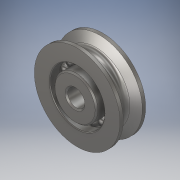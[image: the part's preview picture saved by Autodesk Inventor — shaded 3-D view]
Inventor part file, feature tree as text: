
AUTODESK INVENTOR PART (.ipt)
format: ipt  version: 2019.4 (Build 234330000, 330)  size: 734,208 bytes
history: native  units: in
note: dims shown in document units (in); Inventor stores cm internally (conversion verified against a paired STEP export)
features: other x14, chamfer x2, revolve x1
ambient origin geometry x8: Origin, YZ Plane, XZ Plane, XY Plane, X Axis, Y Axis, Z Axis, Center Point
bodies: Solid1 (feature_tree), Solid2 (feature_tree), Solid3 (feature_tree), Solid4 (feature_tree), Solid5 (feature_tree), Solid6 (feature_tree), Solid7 (feature_tree), Solid8 (feature_tree), Solid9 (feature_tree), Solid10 (feature_tree), Solid11 (feature_tree), Solid12 (feature_tree), Solid13 (feature_tree), Solid14 (feature_tree), Solid15 (feature_tree), Solid16 (feature_tree), Solid17 (feature_tree)
feature tree (17):
  chamfer  "Chamfer2"  [1 undecoded]
  chamfer  "Chamfer1"  [1 undecoded]
  revolve  "Revolve2"  [1 undecoded]
  other  "CirPattern1[1]"
  other  "CirPattern1[2]"
  other  "CirPattern1[3]"
  other  "CirPattern1[4]"
  other  "CirPattern1[5]"
  other  "CirPattern1[6]"
  other  "CirPattern1[7]"
  other  "CirPattern1[8]"
  other  "CirPattern1[9]"
  other  "CirPattern1[10]"
  other  "CirPattern1[11]"
  other  "CirPattern1[12]"
  other  "CirPattern1[13]"
  other  "CirPattern1[14]"
note: 3 required parameter values undecoded (feature->parameter linkage not recoverable at this tier; creation-order binding heuristic only, values carry confidence <= 0.55)
